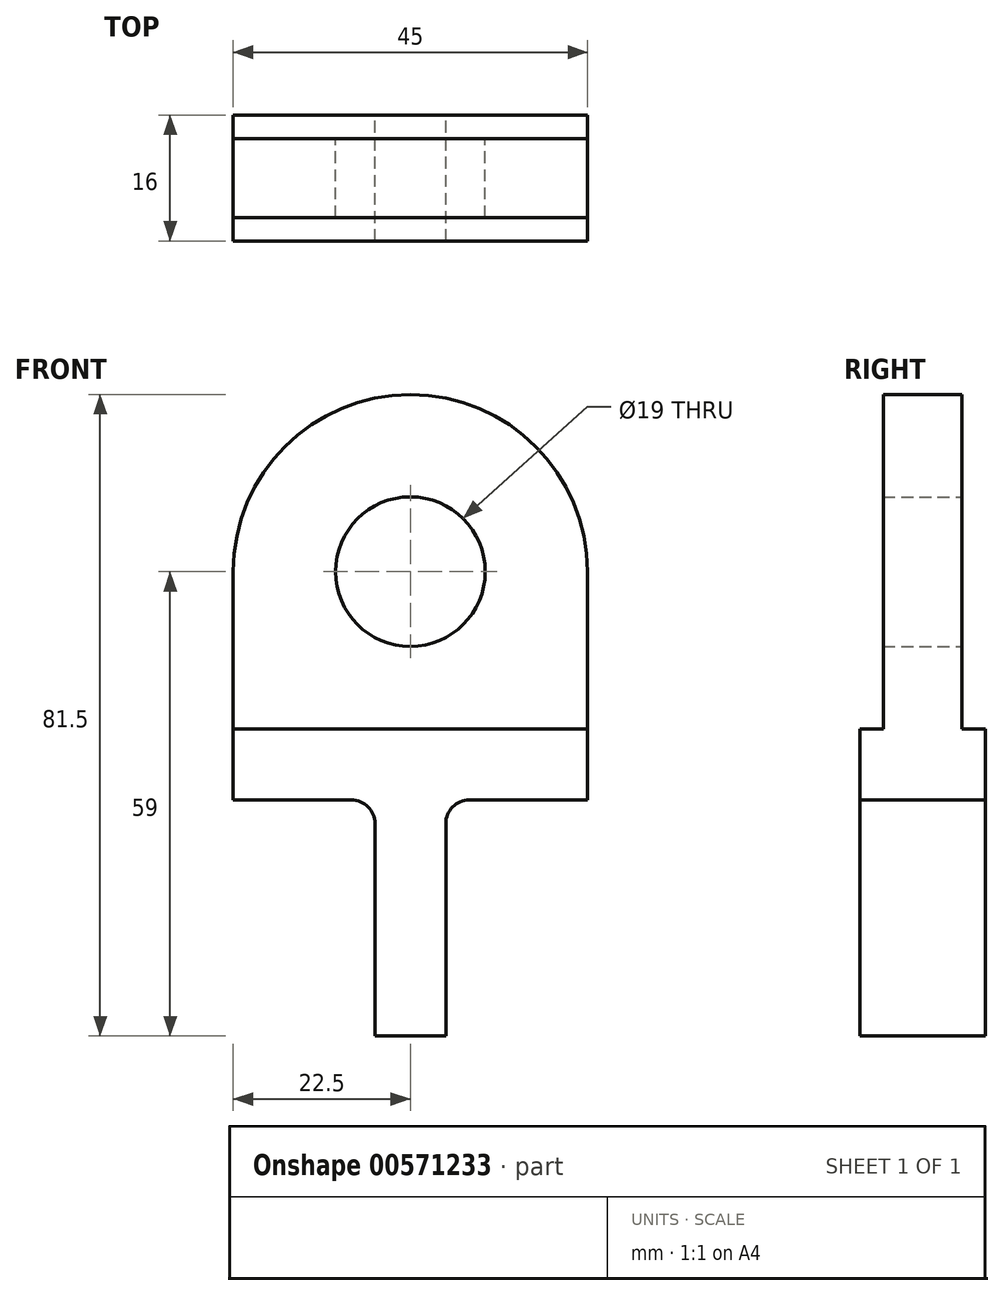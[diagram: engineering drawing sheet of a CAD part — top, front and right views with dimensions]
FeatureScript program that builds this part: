
annotation { "Feature Type Name" : "Feature", "Feature Type Description" : "" }
export const myFeature = defineFeature(function(context is Context, id is Id, definition is map)
    precondition{}
    {
        {
            var Q0;
            Q0=qCreatedBy(makeId("Front.planeOp"),FACE);
            var sketch = newSketch(context, id + "F0", { "sketchPlane" : qUnion([Q0])});
            skCircle(sketch, "E0", {"center": v(0, 0) * mm, "radius": 9.5 * mm});
            skLineSegment(sketch, "E1", {"start": v(0, 0) * mm, "end": v(0, -59) * mm, "construction": true});
            skLineSegment(sketch, "E2", {"start": v(-37.68, 0) * mm, "end": v(40, 0) * mm, "construction": true});
            skArc(sketch, "E3", {"start": v(22.5, 0) * mm, "mid": v(0, 22.5) * mm, "end": v(-22.5, 0) * mm});
            skLineSegment(sketch, "E4", {"start": v(0, -59) * mm, "end": v(4.5, -59) * mm});
            skLineSegment(sketch, "E5", {"start": v(0, -59) * mm, "end": v(-4.5, -59) * mm});
            skLineSegment(sketch, "E6", {"start": v(-4.5, -59) * mm, "end": v(-4.5, -32) * mm});
            skLineSegment(sketch, "E7", {"start": v(4.5, -59) * mm, "end": v(4.5, -32) * mm});
            skLineSegment(sketch, "E8", {"start": v(7.5, -29) * mm, "end": v(22.5, -29) * mm});
            skLineSegment(sketch, "E9", {"start": v(22.5, 0) * mm, "end": v(22.5, -29) * mm});
            skLineSegment(sketch, "E10", {"start": v(-22.5, 0) * mm, "end": v(-22.5, -29) * mm});
            skLineSegment(sketch, "E11", {"start": v(-7.5, -29) * mm, "end": v(-22.5, -29) * mm});
            skArc(sketch, "E12.filletArc", {"start": v(7.5, -29) * mm, "mid": v(5.38, -29.88) * mm, "end": v(4.5, -32) * mm});
            skArc(sketch, "E13.filletArc", {"start": v(-4.5, -32) * mm, "mid": v(-5.38, -29.88) * mm, "end": v(-7.5, -29) * mm});
            skLineSegment(sketch, "E14", {"start": v(-22.5, -29) * mm, "end": v(-22.5, -20) * mm});
            skLineSegment(sketch, "E15", {"start": v(-22.5, -20) * mm, "end": v(22.5, -20) * mm});
            skSolve(sketch);
        }
        {
            var Q0;
            Q0=makeQuery(id+"F0.imprint","IMPRINT",FACE,{"disambiguationData":[TD([[makeQuery(id+"F0.imprint","IMPRINT",EDGE,{"derivedFrom":sQuery(id+"F0.wireOp",EDGE,"E4")}),1.0]])]});
            extrude(context, id + "F1", {"entities" : qUnion([Q0]), "endBound" : BoundingType.SYMMETRIC, "depth" : 16 * mm, "offsetDistance" : 25 * mm});
        }
        {
            var Q0;
            Q0=makeQuery(id+"F0.imprint","IMPRINT",FACE,{"disambiguationData":[TD([[makeQuery(id+"F0.imprint","IMPRINT",EDGE,{"derivedFrom":sQuery(id+"F0.wireOp",EDGE,"E0")}),-1.0]])]});
            extrude(context, id + "F2", {"entities" : qUnion([Q0]), "operationType" : NewBodyOperationType.ADD, "endBound" : BoundingType.SYMMETRIC, "depth" : 10 * mm, "offsetDistance" : 25 * mm});
        }
    });
